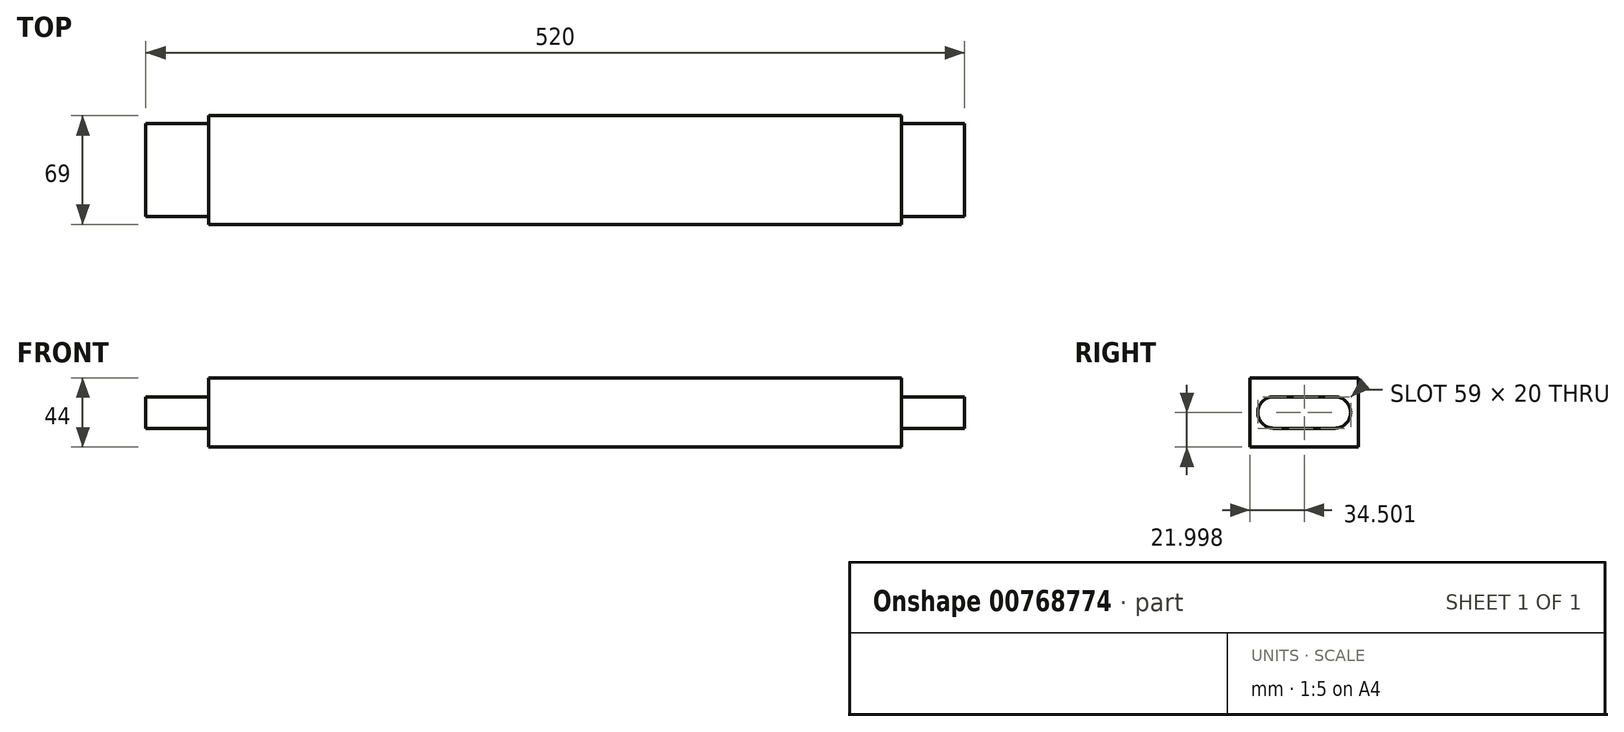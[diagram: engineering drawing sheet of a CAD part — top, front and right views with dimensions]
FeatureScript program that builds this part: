
annotation { "Feature Type Name" : "Feature", "Feature Type Description" : "" }
export const myFeature = defineFeature(function(context is Context, id is Id, definition is map)
    precondition{}
    {
        {
            var Q0;
            Q0=qCreatedBy(makeId("Right.planeOp"),FACE);
            var sketch = newSketch(context, id + "F0", { "sketchPlane" : qUnion([Q0])});
            skLineSegment(sketch, "E0.bottom", {"start": v(-37.66, 7.46) * mm, "end": v(31.34, 7.46) * mm});
            skLineSegment(sketch, "E0.top", {"start": v(-37.66, -36.54) * mm, "end": v(31.34, -36.54) * mm});
            skLineSegment(sketch, "E0.left", {"start": v(-37.66, 7.46) * mm, "end": v(-37.66, -36.54) * mm});
            skLineSegment(sketch, "E0.right", {"start": v(31.34, 7.46) * mm, "end": v(31.34, -36.54) * mm});
            skSolve(sketch);
        }
        {
            var Q0;
            Q0=makeQuery(id+"F0.imprint","IMPRINT",FACE,{"disambiguationData":[TD([[makeQuery(id+"F0.imprint","IMPRINT",EDGE,{"derivedFrom":sQuery(id+"F0.wireOp",EDGE,"E0.bottom")}),-1.0]])]});
            extrude(context, id + "F1", {"entities" : qUnion([Q0]), "depth" : 440 * mm, "offsetDistance" : 25 * mm});
        }
        {
            var Q0;
            Q0=makeQuery(id+"F1.opExtrude","CAP_FACE",FACE,{"disambiguationData":[OSD([sQuery(id+"F0.wireOp",EDGE,"E0.bottom"),sQuery(id+"F0.wireOp",EDGE,"E0.top"),sQuery(id+"F0.wireOp",EDGE,"E0.left"),sQuery(id+"F0.wireOp",EDGE,"E0.right")])],"isStart":true});
            var sketch = newSketch(context, id + "F2", { "sketchPlane" : qUnion([Q0])});
            skLineSegment(sketch, "E1.bottom", {"start": v(-16.34, -24.54) * mm, "end": v(22.66, -24.54) * mm});
            skLineSegment(sketch, "E1.top", {"start": v(-16.34, -4.54) * mm, "end": v(22.66, -4.54) * mm});
            skArc(sketch, "E2", {"start": v(22.66, -24.54) * mm, "mid": v(32.66, -14.54) * mm, "end": v(22.66, -4.54) * mm});
            skArc(sketch, "E3", {"start": v(-16.34, -4.54) * mm, "mid": v(-26.34, -14.54) * mm, "end": v(-16.34, -24.54) * mm});
            skSolve(sketch);
        }
        {
            var Q0;
            Q0=makeQuery(id+"F2.imprint","IMPRINT",FACE,{"disambiguationData":[TD([[makeQuery(id+"F2.imprint","IMPRINT",EDGE,{"derivedFrom":sQuery(id+"F2.wireOp",EDGE,"E1.bottom")}),1.0]])]});
            extrude(context, id + "F3", {"entities" : qUnion([Q0]), "operationType" : NewBodyOperationType.ADD, "depth" : 40 * mm, "offsetDistance" : 25 * mm});
        }
        {
            var Q0;
            Q0=makeQuery(id+"F1.opExtrude","CAP_FACE",FACE,{"disambiguationData":[OSD([sQuery(id+"F0.wireOp",EDGE,"E0.bottom"),sQuery(id+"F0.wireOp",EDGE,"E0.top"),sQuery(id+"F0.wireOp",EDGE,"E0.left"),sQuery(id+"F0.wireOp",EDGE,"E0.right")])],"isStart":false});
            var sketch = newSketch(context, id + "F4", { "sketchPlane" : qUnion([Q0])});
            skLineSegment(sketch, "E4.bottom", {"start": v(16.34, -4.54) * mm, "end": v(-22.66, -4.54) * mm});
            skLineSegment(sketch, "E4.top", {"start": v(16.34, -24.54) * mm, "end": v(-22.66, -24.54) * mm});
            skArc(sketch, "E5", {"start": v(16.34, -24.54) * mm, "mid": v(26.34, -14.54) * mm, "end": v(16.34, -4.54) * mm});
            skArc(sketch, "E6", {"start": v(-22.66, -4.54) * mm, "mid": v(-32.66, -14.54) * mm, "end": v(-22.66, -24.54) * mm});
            skSolve(sketch);
        }
        {
            var Q0;
            Q0=makeQuery(id+"F4.imprint","IMPRINT",FACE,{"disambiguationData":[TD([[makeQuery(id+"F4.imprint","IMPRINT",EDGE,{"derivedFrom":sQuery(id+"F4.wireOp",EDGE,"E4.bottom")}),1.0]])]});
            extrude(context, id + "F5", {"entities" : qUnion([Q0]), "operationType" : NewBodyOperationType.ADD, "depth" : 40 * mm, "offsetDistance" : 25 * mm});
        }
    });
